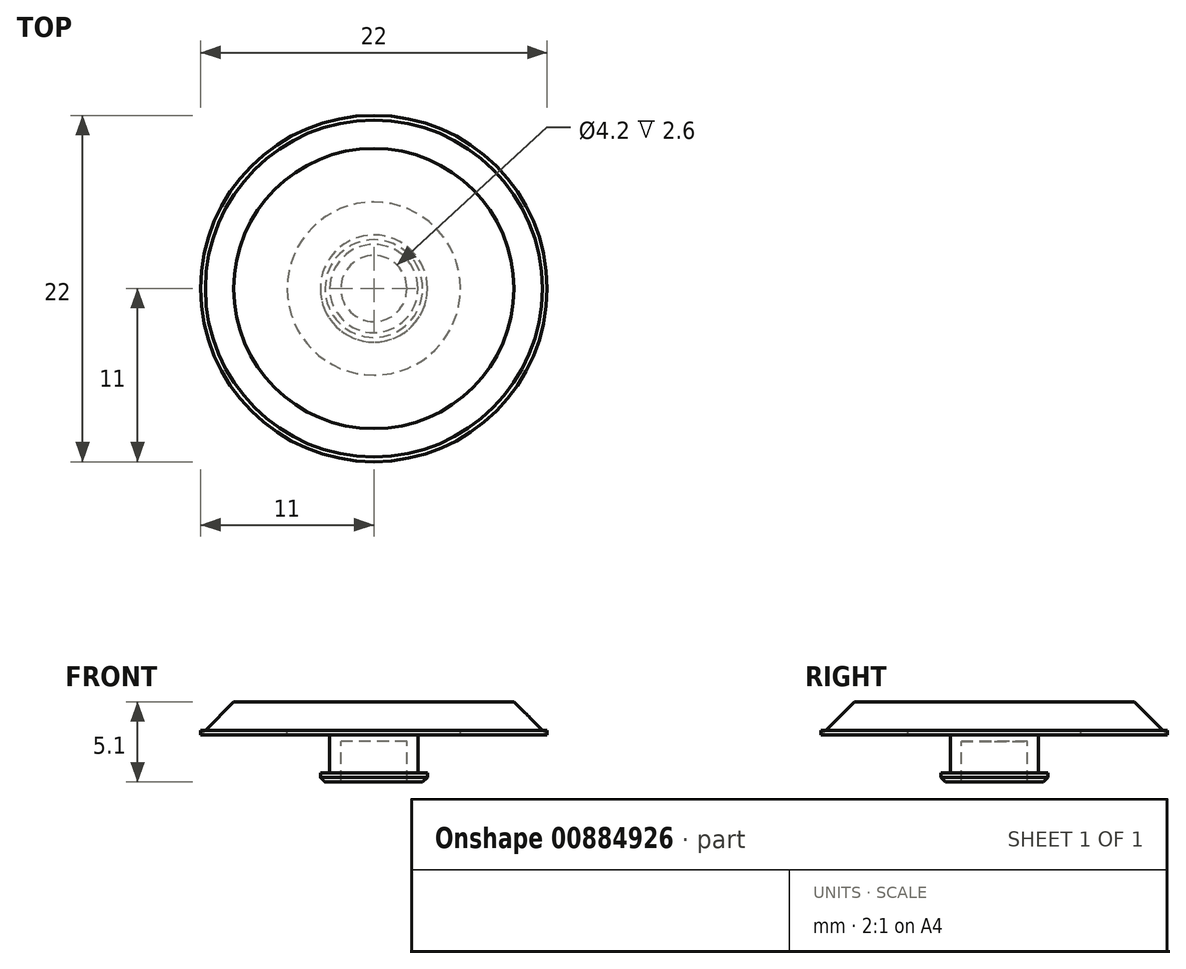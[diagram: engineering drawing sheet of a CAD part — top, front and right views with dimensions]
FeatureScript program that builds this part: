
annotation { "Feature Type Name" : "Feature", "Feature Type Description" : "" }
export const myFeature = defineFeature(function(context is Context, id is Id, definition is map)
    precondition{}
    {
        {
            var Q0;
            Q0=qCreatedBy(makeId("Front.planeOp"),FACE);
            var sketch = newSketch(context, id + "F0", { "sketchPlane" : qUnion([Q0])});
            skLineSegment(sketch, "E0", {"start": v(-2.8, 0) * mm, "end": v(-5.5, 0) * mm});
            skLineSegment(sketch, "E1", {"start": v(-5.5, 0) * mm, "end": v(-5.5, 0.3) * mm});
            skLineSegment(sketch, "E2", {"start": v(-5.5, 0.3) * mm, "end": v(-11, 0.3) * mm});
            skLineSegment(sketch, "E3", {"start": v(-11, 0) * mm, "end": v(-11, 0.3) * mm});
            skLineSegment(sketch, "E4", {"start": v(0, 0.45) * mm, "end": v(0, 0.45) * mm});
            skLineSegment(sketch, "E5", {"start": v(-8.9, 2.1) * mm, "end": v(-11, 0) * mm});
            skLineSegment(sketch, "E6", {"start": v(0, 2.1) * mm, "end": v(0, 2.1) * mm});
            skLineSegment(sketch, "E7", {"start": v(-3.4, -3) * mm, "end": v(-3.4, -2.4) * mm});
            skLineSegment(sketch, "E8", {"start": v(-3.4, -2.4) * mm, "end": v(-2.8, -2.4) * mm});
            skLineSegment(sketch, "E9", {"start": v(-2.8, -2.4) * mm, "end": v(-2.8, 0) * mm});
            skLineSegment(sketch, "E10", {"start": v(-8.9, 2.1) * mm, "end": v(0, 2.1) * mm});
            skLineSegment(sketch, "E11", {"start": v(0, 2.1) * mm, "end": v(0, -0.4) * mm});
            skLineSegment(sketch, "E12", {"start": v(0, 5.84) * mm, "end": v(0, -6.83) * mm, "construction": true});
            skLineSegment(sketch, "E13", {"start": v(-3.4, -3) * mm, "end": v(-2.1, -3) * mm});
            skLineSegment(sketch, "E14", {"start": v(-2.1, -3) * mm, "end": v(-2.1, -0.4) * mm});
            skLineSegment(sketch, "E15", {"start": v(-2.1, -0.4) * mm, "end": v(0, -0.4) * mm});
            skSolve(sketch);
        }
        {
            var Q0;
            Q0 = qSketchRegion(id + "F0", true);
            var Q1;
            Q1=sQuery(id+"F0.wireOp",EDGE,"E12");
            revolve(context, id + "F1", {"surfaceOperationType" : NewSurfaceOperationType.NEW, "entities" : qUnion([Q0]), "axis" : qUnion([Q1]), "revolveType" : RevolveType.FULL});
        }
        {
            var Q0;
            Q0=makeQuery(id+"F1.opRevolve","SWEPT_EDGE",EDGE,{"disambiguationData":[OSD([sQuery(id+"F0.wireOp",EDGE,"E7"),sQuery(id+"F0.wireOp",EDGE,"E13")])]});
            chamfer(context, id + "F2", {"entities" : qUnion([Q0]), "width" : .3 * mm, "tangentPropagation" : true});
        }
    });
